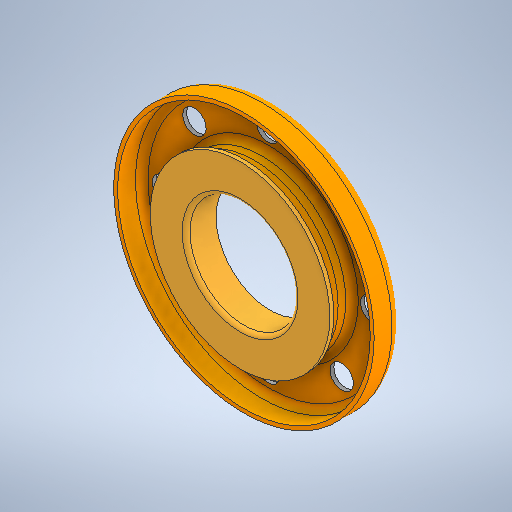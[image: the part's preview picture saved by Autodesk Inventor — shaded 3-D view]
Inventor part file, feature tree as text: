
AUTODESK INVENTOR PART (.ipt)
format: ipt  version: 2025 (Build 290162010, 162A)  size: 420,352 bytes
history: native  units: mm
features: other x12, sketch x3, revolve x2, extrude x1, pattern_circular x1
ambient origin geometry x8: Origin, YZ Plane, XZ Plane, XY Plane, X Axis, Y Axis, Z Axis, Center Point
bodies: Solid1 (feature_tree)
feature tree (19):
  other  "Table"
  other  "Stamp flange DIN2642-015"
  other  "Stamp flange DIN2642-020"
  other  "Stamp flange DIN2642-025"
  other  "Stamp flange DIN2642-032"
  other  "Stamp flange DIN2642-040"
  other  "Stamp flange DIN2642-050"
  other  "Stamp flange DIN2642-065"
  other  "Stamp flange DIN2642-080"
  other  "Stamp flange DIN2642-100"
  other  "Stamp flange DIN2642-125"
  other  "Stamp flange DIN2642-150"
  revolve  "Revolution1"  [1 undecoded]
  revolve  "Revolution2"  Angle=90.0deg
  extrude  "Extrusion1"  TaperAngle=360.0deg  [1 undecoded]
  pattern_circular  "Circular Pattern1"  [2 undecoded]
  sketch  "Sketch1"  dims[d7=90.0deg d8=3.0mm]
  sketch  "Sketch2"  dims[d10=4.8125mm d15=90.0deg]
  sketch  "Sketch3"  dims[d18=0.0mm d19=0.0mm d21=360.0deg d23=38.5mm d26=3.0mm]
note: 4 required parameter values undecoded (feature->parameter linkage not recoverable at this tier; creation-order binding heuristic only, values carry confidence <= 0.55)